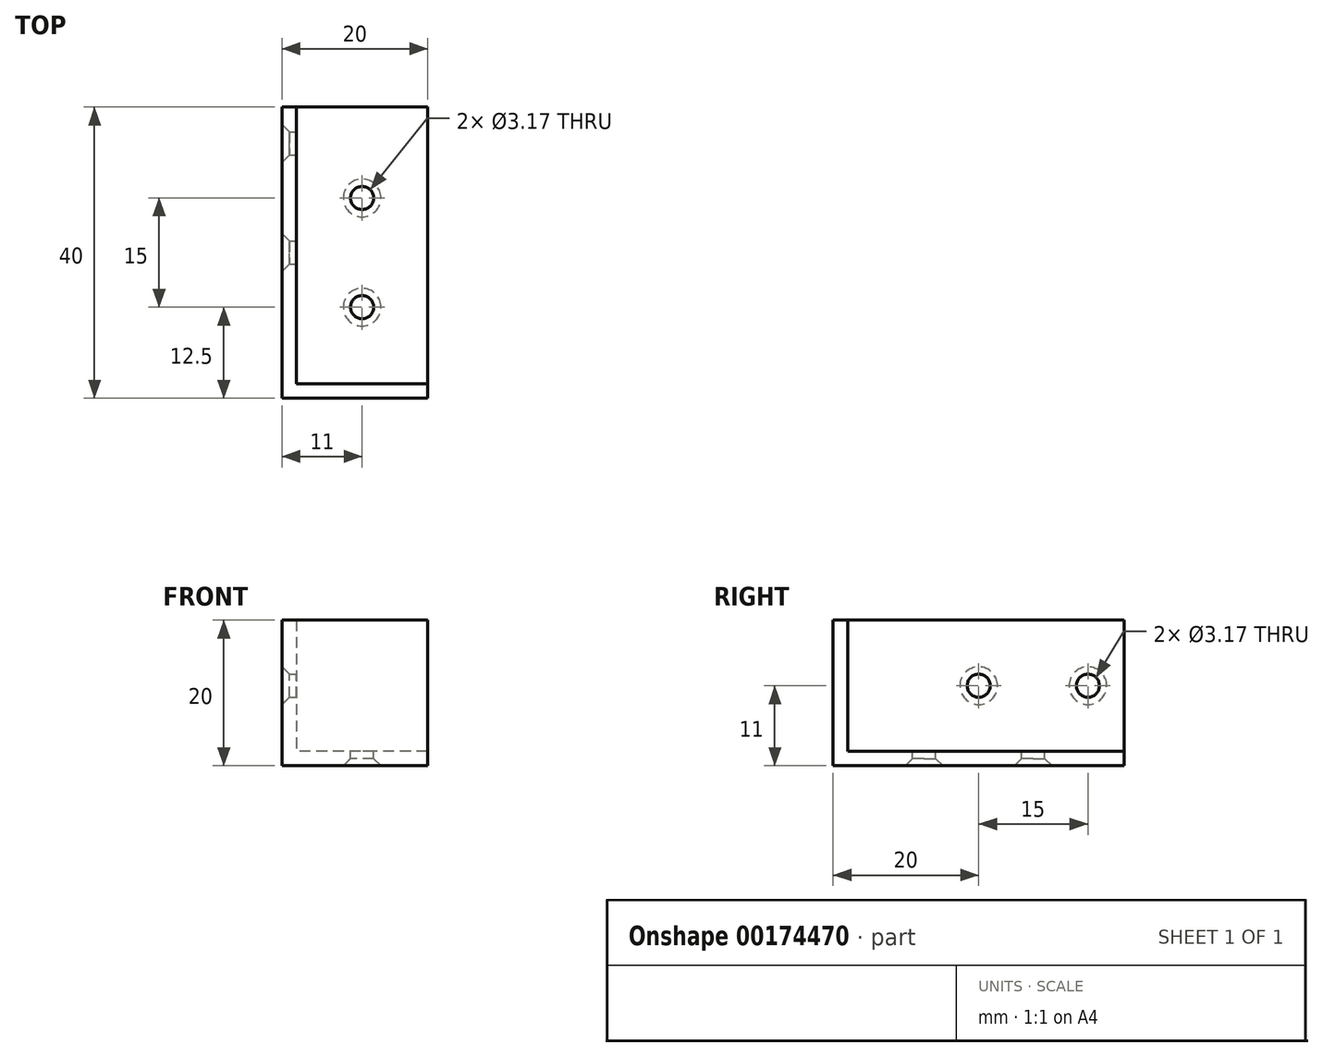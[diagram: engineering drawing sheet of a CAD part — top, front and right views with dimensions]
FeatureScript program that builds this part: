
annotation { "Feature Type Name" : "Feature", "Feature Type Description" : "" }
export const myFeature = defineFeature(function(context is Context, id is Id, definition is map)
    precondition{}
    {
        {
            var Q0;
            Q0=qCreatedBy(makeId("Front.planeOp"),FACE);
            var sketch = newSketch(context, id + "F0", { "sketchPlane" : qUnion([Q0])});
            skLineSegment(sketch, "E0", {"start": v(-2, -2) * mm, "end": v(-2, 18) * mm});
            skLineSegment(sketch, "E1", {"start": v(-2, 18) * mm, "end": v(0, 18) * mm});
            skLineSegment(sketch, "E2", {"start": v(-2, -2) * mm, "end": v(18, -2) * mm});
            skLineSegment(sketch, "E3", {"start": v(0, 18) * mm, "end": v(0, 0) * mm});
            skLineSegment(sketch, "E4", {"start": v(0, 0) * mm, "end": v(18, 0) * mm});
            skLineSegment(sketch, "E5", {"start": v(18, 0) * mm, "end": v(18, -2) * mm});
            skSolve(sketch);
        }
        {
            var Q0;
            Q0=makeQuery(id+"F0.imprint","IMPRINT",FACE,{"disambiguationData":[TD([[makeQuery(id+"F0.imprint","IMPRINT",EDGE,{"derivedFrom":sQuery(id+"F0.wireOp",EDGE,"E0")}),-1.0]])]});
            extrude(context, id + "F1", {"entities" : qUnion([Q0]), "oppositeDirection" : true, "depth" : 40 * mm});
        }
        {
            var Q0;
            Q0=makeQuery(id+"F1.opExtrude","SWEPT_FACE",FACE,{"disambiguationData":[OSD([sQuery(id+"F0.wireOp",EDGE,"BLrCOVyg-vFY3-6Uj6-42PL-0wbM1FOnHA4J"),sQuery(id+"F0.wireOp",EDGE,"E3")])]});
            var sketch = newSketch(context, id + "F2", { "sketchPlane" : qUnion([Q0])});
            skLineSegment(sketch, "E6.bottom", {"start": v(0, 18) * mm, "end": v(2, 18) * mm});
            skLineSegment(sketch, "E6.top", {"start": v(0, 0) * mm, "end": v(2, 0) * mm});
            skLineSegment(sketch, "E6.left", {"start": v(0, 18) * mm, "end": v(0, 0) * mm});
            skLineSegment(sketch, "E6.right", {"start": v(2, 18) * mm, "end": v(2, 0) * mm});
            skSolve(sketch);
        }
        {
            var Q0;
            Q0=qSketchRegion(id+"F2",true);
            var Q1;
            Q1=makeQuery(id+"F1.opExtrude","SWEPT_FACE",FACE,{"disambiguationData":[OSD([sQuery(id+"F0.wireOp",EDGE,"E5")])]});
            extrude(context, id + "F3", {"entities" : qUnion([Q0]), "operationType" : NewBodyOperationType.ADD, "endBound" : BoundingType.UP_TO_SURFACE, "endBoundEntityFace" : qUnion([Q1]), "depth" : 25 * mm});
        }
        {
            var Q0;
            Q0=makeQuery(id+"F1.opExtrude","SWEPT_FACE",FACE,{"disambiguationData":[OSD([sQuery(id+"F0.wireOp",EDGE,"E4")])]});
            var sketch = newSketch(context, id + "F4", { "sketchPlane" : qUnion([Q0])});
            skLineSegment(sketch, "E7", {"start": v(9, 40) * mm, "end": v(9, 27.5) * mm, "construction": true});
            skLineSegment(sketch, "E8", {"start": v(9, 27.5) * mm, "end": v(9, 12.5) * mm, "construction": true});
            skCircle(sketch, "E9", {"center": v(9, 27.5) * mm, "radius": 1.59 * mm});
            skCircle(sketch, "E10", {"center": v(9, 12.5) * mm, "radius": 1.59 * mm});
            skSolve(sketch);
        }
        {
            var Q0;
            Q0=makeQuery(id+"F4.imprint","IMPRINT",FACE,{"disambiguationData":[TD([[makeQuery(id+"F4.imprint","IMPRINT",EDGE,{"derivedFrom":sQuery(id+"F4.wireOp",EDGE,"E10")}),1.0]])]});
            var Q1;
            Q1=makeQuery(id+"F4.imprint","IMPRINT",FACE,{"disambiguationData":[TD([[makeQuery(id+"F4.imprint","IMPRINT",EDGE,{"derivedFrom":sQuery(id+"F4.wireOp",EDGE,"E9")}),1.0]])]});
            extrude(context, id + "F5", {"entities" : qUnion([Q0, Q1]), "operationType" : NewBodyOperationType.REMOVE, "endBound" : BoundingType.THROUGH_ALL, "oppositeDirection" : true, "depth" : 25 * mm});
        }
        {
            var Q0;
            Q0=makeQuery(id+"F1.opExtrude","SWEPT_FACE",FACE,{"disambiguationData":[OSD([sQuery(id+"F0.wireOp",EDGE,"E3")])]});
            var sketch = newSketch(context, id + "F6", { "sketchPlane" : qUnion([Q0])});
            skLineSegment(sketch, "E11", {"start": v(40, 9) * mm, "end": v(35, 9) * mm, "construction": true});
            skLineSegment(sketch, "E12", {"start": v(35, 9) * mm, "end": v(20, 9) * mm, "construction": true});
            skCircle(sketch, "E13", {"center": v(35, 9) * mm, "radius": 1.59 * mm});
            skCircle(sketch, "E14", {"center": v(20, 9) * mm, "radius": 1.59 * mm});
            skSolve(sketch);
        }
        {
            var Q0;
            Q0=qSketchRegion(id+"F6",true);
            extrude(context, id + "F7", {"entities" : qUnion([Q0]), "operationType" : NewBodyOperationType.REMOVE, "endBound" : BoundingType.THROUGH_ALL, "oppositeDirection" : true, "depth" : 25 * mm});
        }
        {
            var Q0;
            Q0=makeQuery(id+"F7.boolean.opBoolean","INTERSECT",EDGE,{"derivedFrom":[makeQuery(id+"F1.opExtrude","SWEPT_FACE",FACE,{"disambiguationData":[OSD([sQuery(id+"F0.wireOp",EDGE,"E0")])]}),makeQuery(id+"F7.opExtrude","SWEPT_FACE",FACE,{"disambiguationData":[OSD([sQuery(id+"F6.wireOp",EDGE,"E14")])]})]});
            var Q1;
            Q1=makeQuery(id+"F7.boolean.opBoolean","INTERSECT",EDGE,{"derivedFrom":[makeQuery(id+"F1.opExtrude","SWEPT_FACE",FACE,{"disambiguationData":[OSD([sQuery(id+"F0.wireOp",EDGE,"E0")])]}),makeQuery(id+"F7.opExtrude","SWEPT_FACE",FACE,{"disambiguationData":[OSD([sQuery(id+"F6.wireOp",EDGE,"E13")])]})]});
            var Q2;
            Q2=makeQuery(id+"F5.boolean.opBoolean","INTERSECT",EDGE,{"derivedFrom":[makeQuery(id+"F1.opExtrude","SWEPT_FACE",FACE,{"disambiguationData":[OSD([sQuery(id+"F0.wireOp",EDGE,"E2")])]}),makeQuery(id+"F5.opExtrude","SWEPT_FACE",FACE,{"disambiguationData":[OSD([sQuery(id+"F4.wireOp",EDGE,"E9")])]})]});
            var Q3;
            Q3=makeQuery(id+"F5.boolean.opBoolean","INTERSECT",EDGE,{"derivedFrom":[makeQuery(id+"F1.opExtrude","SWEPT_FACE",FACE,{"disambiguationData":[OSD([sQuery(id+"F0.wireOp",EDGE,"E2")])]}),makeQuery(id+"F5.opExtrude","SWEPT_FACE",FACE,{"disambiguationData":[OSD([sQuery(id+"F4.wireOp",EDGE,"E10")])]})]});
            chamfer(context, id + "F8", {"entities" : qUnion([Q0, Q1, Q2, Q3]), "width" : 1 * mm, "tangentPropagation" : true});
        }
    });
